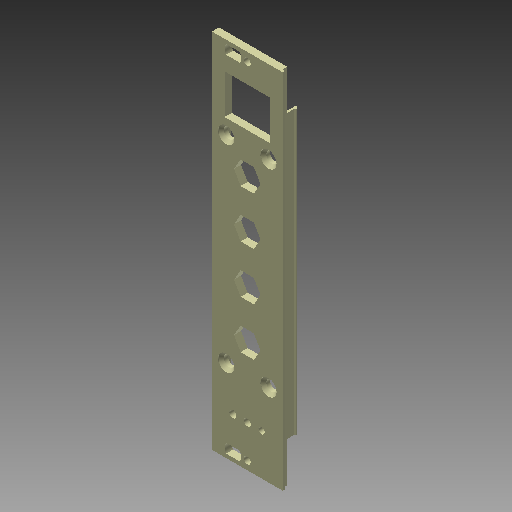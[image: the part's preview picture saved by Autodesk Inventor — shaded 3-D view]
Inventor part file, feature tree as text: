
AUTODESK INVENTOR PART (.ipt)
format: ipt  version: 2017 (Build 210142000, 142)  size: 255,488 bytes
history: native  units: in
note: dims shown in document units (in); Inventor stores cm internally (conversion verified against a paired STEP export)
features: extrude x2, sketch x1, other x1
ambient origin geometry x8: Origin, YZ Plane, XZ Plane, XY Plane, X Axis, Y Axis, Z Axis, Center Point
bodies: Solid1 (feature_tree)
feature tree (4):
  extrude  "Extrusion1"  TaperAngle=90.0deg  [1 undecoded]
  extrude  "Extrusion2"  Depth=0.4931in
  sketch  "Sketch1"  dims[d0=0.3701in d1=90.0deg d3=0.4931in d4=0.1969in d5=1.5748in d7=0.6693in d8=0.3937in d10=0.3937in d12=0.3937in d13=0.0in d14=0.6323in d15=0.5512in d16=0.1772in d17=0.3937in d18=0.0in d19=0.0in]
  other  "rj45"
note: 1 required parameter value undecoded (feature->parameter linkage not recoverable at this tier; creation-order binding heuristic only, values carry confidence <= 0.55)
